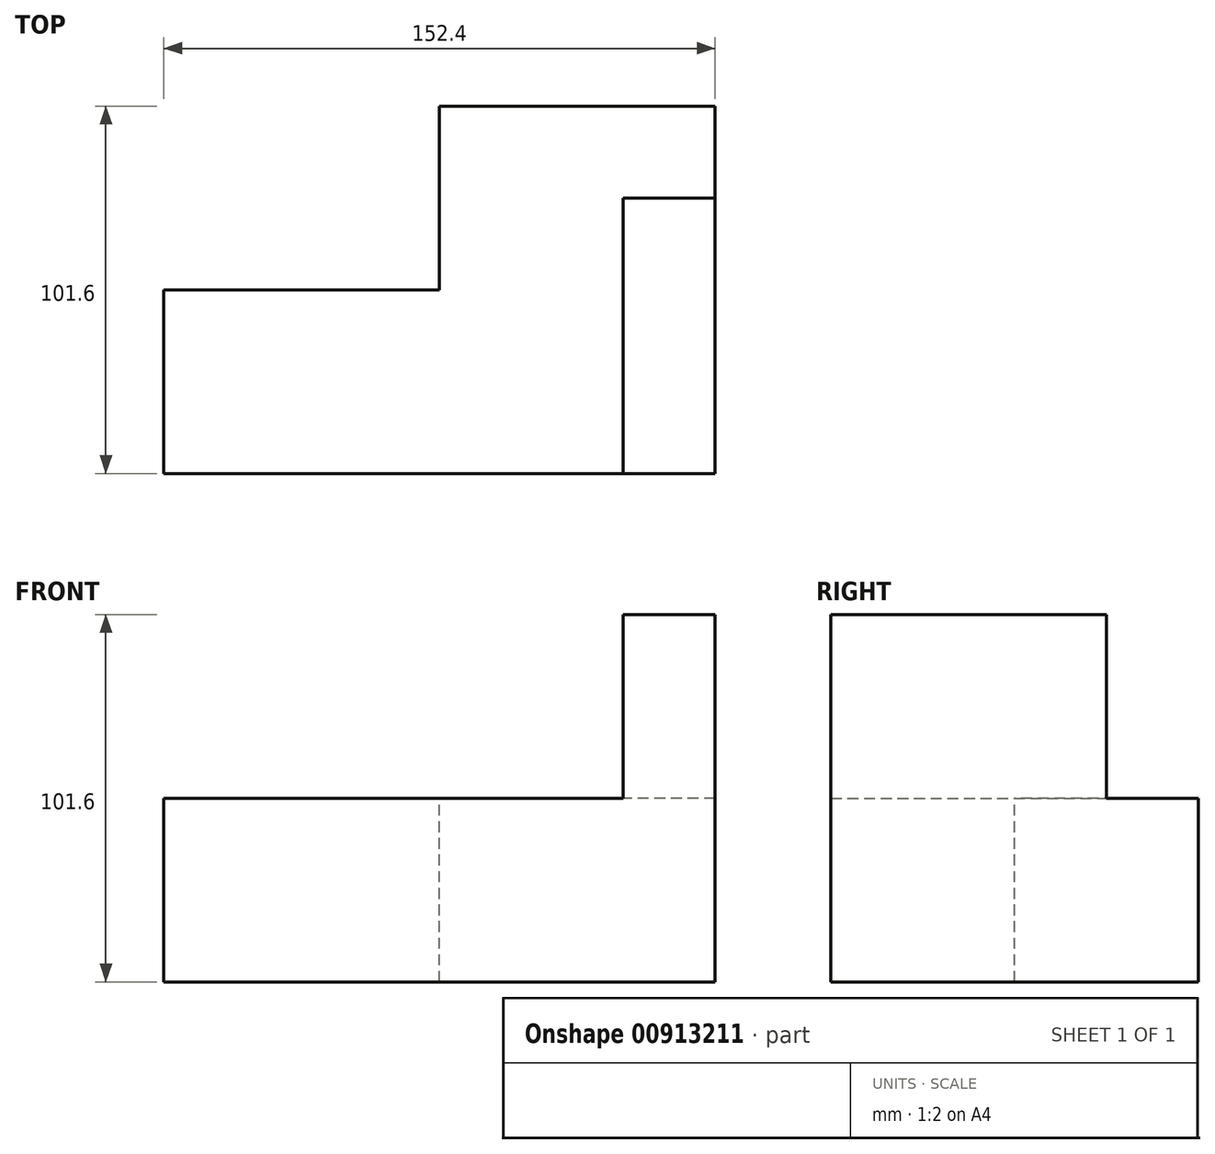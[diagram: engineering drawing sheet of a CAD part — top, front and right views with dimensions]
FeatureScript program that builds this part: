
annotation { "Feature Type Name" : "Feature", "Feature Type Description" : "" }
export const myFeature = defineFeature(function(context is Context, id is Id, definition is map)
    precondition{}
    {
        {
            var Q0;
            Q0=qCreatedBy(makeId("Top.planeOp"),FACE);
            var sketch = newSketch(context, id + "F0", { "sketchPlane" : qUnion([Q0])});
            skLineSegment(sketch, "E0.bottom", {"start": v(0, 0) * mm, "end": v(-152.4, 0) * mm});
            skLineSegment(sketch, "E0.top", {"start": v(0, 101.6) * mm, "end": v(-152.4, 101.6) * mm});
            skLineSegment(sketch, "E0.left", {"start": v(0, 0) * mm, "end": v(0, 101.6) * mm});
            skLineSegment(sketch, "E0.right", {"start": v(-152.4, 0) * mm, "end": v(-152.4, 101.6) * mm});
            skSolve(sketch);
        }
        {
            var Q0;
            Q0=makeQuery(id+"F0.imprint","IMPRINT",FACE,{"disambiguationData":[TD([[makeQuery(id+"F0.imprint","IMPRINT",EDGE,{"derivedFrom":sQuery(id+"F0.wireOp",EDGE,"E0.bottom")}),-1.0]])]});
            extrude(context, id + "F1", {"entities" : qUnion([Q0]), "depth" : 50.8 * mm, "offsetDistance" : 25.4 * mm});
        }
        {
            var Q0;
            Q0=makeQuery(id+"F1.opExtrude","CAP_FACE",FACE,{"disambiguationData":[OSD([sQuery(id+"F0.wireOp",EDGE,"E0.bottom"),sQuery(id+"F0.wireOp",EDGE,"E0.top"),sQuery(id+"F0.wireOp",EDGE,"E0.left"),sQuery(id+"F0.wireOp",EDGE,"E0.right")])],"isStart":false});
            var sketch = newSketch(context, id + "F2", { "sketchPlane" : qUnion([Q0])});
            skLineSegment(sketch, "E1.bottom", {"start": v(0, 0) * mm, "end": v(-25.4, 0) * mm});
            skLineSegment(sketch, "E1.top", {"start": v(0, 76.2) * mm, "end": v(-25.4, 76.2) * mm});
            skLineSegment(sketch, "E1.left", {"start": v(0, 0) * mm, "end": v(0, 76.2) * mm});
            skLineSegment(sketch, "E1.right", {"start": v(-25.4, 0) * mm, "end": v(-25.4, 76.2) * mm});
            skSolve(sketch);
        }
        {
            var Q0;
            Q0 = qSketchRegion(id + "F2", true);
            extrude(context, id + "F3", {"entities" : qUnion([Q0]), "operationType" : NewBodyOperationType.ADD, "depth" : 50.8 * mm, "offsetDistance" : 25.4 * mm});
        }
        {
            var Q0;
            Q0=makeQuery(id+"F1.opExtrude","CAP_FACE",FACE,{"disambiguationData":[OSD([sQuery(id+"F0.wireOp",EDGE,"E0.bottom"),sQuery(id+"F0.wireOp",EDGE,"E0.top"),sQuery(id+"F0.wireOp",EDGE,"E0.left"),sQuery(id+"F0.wireOp",EDGE,"E0.right")])],"isStart":false});
            var sketch = newSketch(context, id + "F4", { "sketchPlane" : qUnion([Q0])});
            skLineSegment(sketch, "E2.bottom", {"start": v(-152.4, 101.6) * mm, "end": v(-76.2, 101.6) * mm});
            skLineSegment(sketch, "E2.top", {"start": v(-152.4, 50.8) * mm, "end": v(-76.2, 50.8) * mm});
            skLineSegment(sketch, "E2.left", {"start": v(-152.4, 101.6) * mm, "end": v(-152.4, 50.8) * mm});
            skLineSegment(sketch, "E2.right", {"start": v(-76.2, 101.6) * mm, "end": v(-76.2, 50.8) * mm});
            skSolve(sketch);
        }
        {
            var Q0;
            Q0 = qSketchRegion(id + "F4", true);
            extrude(context, id + "F5", {"entities" : qUnion([Q0]), "operationType" : NewBodyOperationType.REMOVE, "endBound" : BoundingType.THROUGH_ALL, "oppositeDirection" : true, "depth" : 25.4 * mm, "offsetDistance" : 25.4 * mm});
        }
    });
